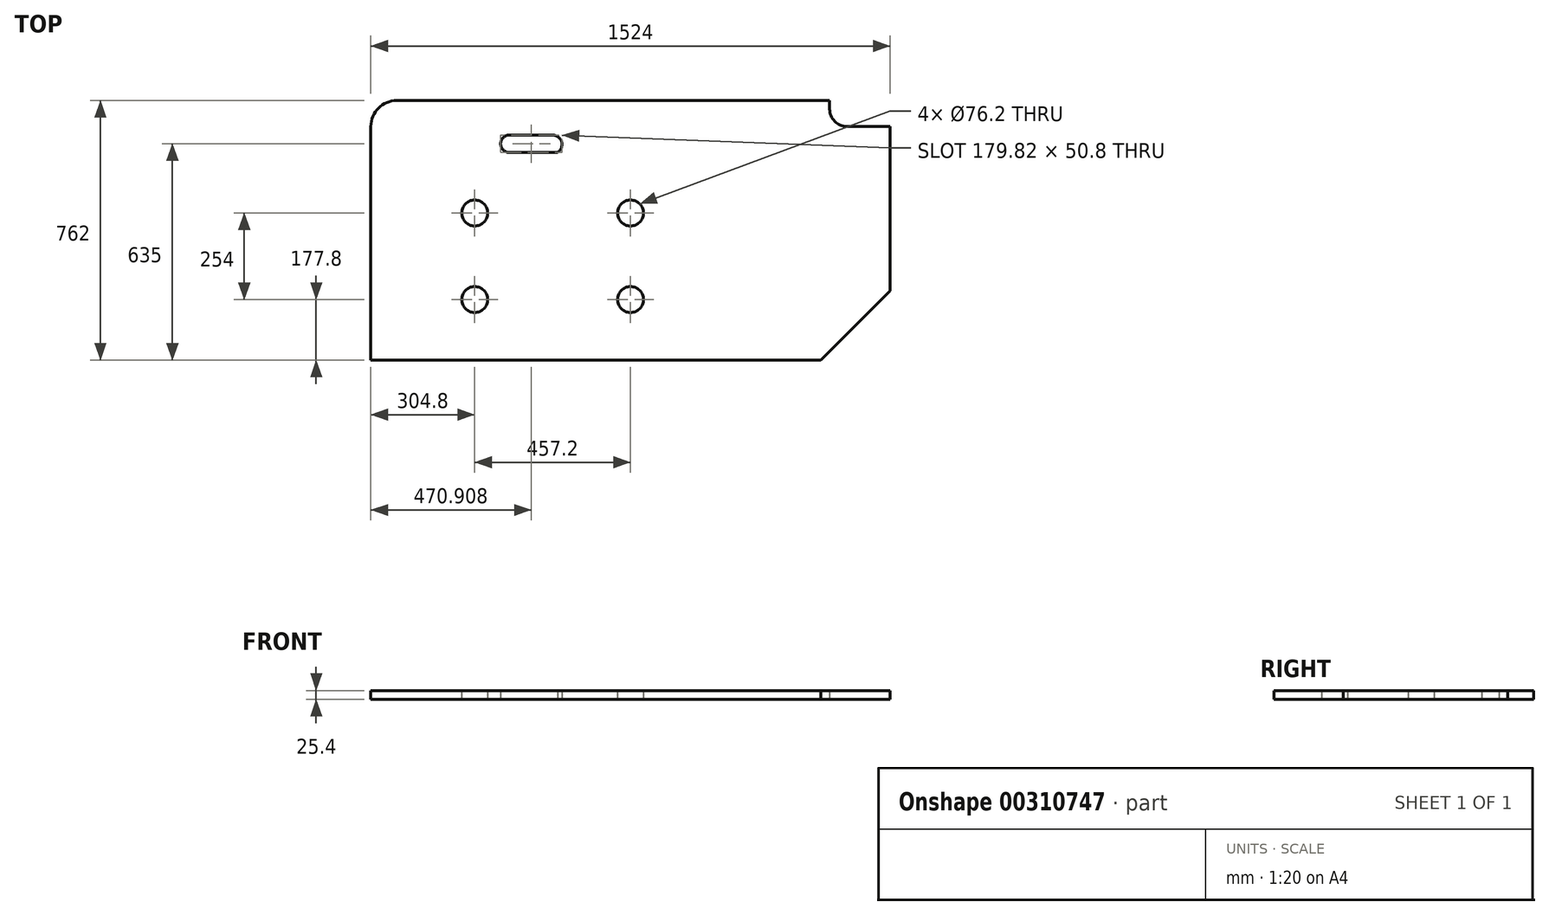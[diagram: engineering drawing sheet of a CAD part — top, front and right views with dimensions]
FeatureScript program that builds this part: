
annotation { "Feature Type Name" : "Feature", "Feature Type Description" : "" }
export const myFeature = defineFeature(function(context is Context, id is Id, definition is map)
    precondition{}
    {
        {
            var Q0;
            Q0=qCreatedBy(makeId("Top.planeOp"),FACE);
            var sketch = newSketch(context, id + "F0", { "sketchPlane" : qUnion([Q0])});
            skPoint(sketch, "E0.0", {"position": v(0, 0) * mm});
            skLineSegment(sketch, "E1.bottom", {"start": v(0, 0) * mm, "end": v(1524, 0) * mm});
            skLineSegment(sketch, "E1.top", {"start": v(0, 762) * mm, "end": v(1346.2, 762) * mm});
            skLineSegment(sketch, "E1.left", {"start": v(0, 0) * mm, "end": v(0, 762) * mm});
            skLineSegment(sketch, "E1.right", {"start": v(1524, 0) * mm, "end": v(1524, 685.8) * mm});
            skLineSegment(sketch, "E2.bottom", {"start": v(304.8, 177.8) * mm, "end": v(762, 177.8) * mm, "construction": true});
            skLineSegment(sketch, "E2.top", {"start": v(304.8, 431.8) * mm, "end": v(762, 431.8) * mm, "construction": true});
            skLineSegment(sketch, "E2.left", {"start": v(304.8, 177.8) * mm, "end": v(304.8, 431.8) * mm, "construction": true});
            skLineSegment(sketch, "E2.right", {"start": v(762, 177.8) * mm, "end": v(762, 431.8) * mm, "construction": true});
            skPoint(sketch, "E3", {"position": v(304.8, 177.8) * mm});
            skPoint(sketch, "E4", {"position": v(304.8, 431.8) * mm});
            skPoint(sketch, "E5", {"position": v(762, 431.8) * mm});
            skPoint(sketch, "E6", {"position": v(762, 177.8) * mm});
            skLineSegment(sketch, "E7", {"start": v(1346.2, 762) * mm, "end": v(1346.2, 685.8) * mm});
            skLineSegment(sketch, "E8", {"start": v(1346.2, 685.8) * mm, "end": v(1524, 685.8) * mm});
            skSolve(sketch);
        }
        {
            var Q0;
            Q0=makeQuery(id+"F0.imprint","IMPRINT",FACE,{"disambiguationData":[TD([[makeQuery(id+"F0.imprint","IMPRINT",EDGE,{"derivedFrom":sQuery(id+"F0.wireOp",EDGE,"E1.bottom")}),1.0]])]});
            extrude(context, id + "F1", {"entities" : qUnion([Q0]), "depth" : 25.4 * mm, "offsetDistance" : 25.4 * mm});
        }
        {
            var Q0;
            Q0=sQuery(id+"F0.wireOp",VERTEX,"E3");
            var Q1;
            Q1=sQuery(id+"F0.wireOp",VERTEX,"E4");
            var Q2;
            Q2=sQuery(id+"F0.wireOp",VERTEX,"E5");
            var Q3;
            Q3=sQuery(id+"F0.wireOp",VERTEX,"E6");
            var Q4;
            Q4=makeQuery(id+"F1.opExtrude","SWEPT_BODY",BODY,{"disambiguationData":[OSD([sQuery(id+"F0.wireOp",EDGE,"E1.bottom"),sQuery(id+"F0.wireOp",EDGE,"E1.top"),sQuery(id+"F0.wireOp",EDGE,"E1.left"),sQuery(id+"F0.wireOp",EDGE,"E1.right")])]});
            hole(context, id + "F2", {"style" : HoleStyle.SIMPLE, "endStyle" : HoleEndStyle.THROUGH, "oppositeDirection" : true, "holeDiameter" : 76.2 * mm, "majorDiameter" : 6.35 * mm, "isTappedThrough" : true, "tappedDepth" : 12.7 * mm, "tapClearance" : 3, "locations" : qUnion([Q0, Q1, Q2, Q3]), "scope" : qUnion([Q4])});
        }
        {
            var Q0;
            Q0=makeQuery(id+"F1.opExtrude","SWEPT_EDGE",EDGE,{"disambiguationData":[OSD([sQuery(id+"F0.wireOp",EDGE,"E1.top"),sQuery(id+"F0.wireOp",EDGE,"E1.left")])]});
            fillet(context, id + "F3", {"entities" : qUnion([Q0]), "tangentPropagation" : true, "radius" : 76.2 * mm, "defaultsChanged" : true, "vertexSettings" : [], "allowEdgeOverflow" : false});
        }
        {
            var Q0;
            Q0=makeQuery(id+"F1.opExtrude","SWEPT_EDGE",EDGE,{"disambiguationData":[OSD([sQuery(id+"F0.wireOp",EDGE,"E1.bottom"),sQuery(id+"F0.wireOp",EDGE,"E1.right")])]});
            chamfer(context, id + "F4", {"entities" : qUnion([Q0]), "width" : 203.2 * mm, "tangentPropagation" : true});
        }
        {
            var Q0;
            Q0=makeQuery(id+"F1.opExtrude","SWEPT_EDGE",EDGE,{"disambiguationData":[OSD([sQuery(id+"F0.wireOp",EDGE,"E7"),sQuery(id+"F0.wireOp",EDGE,"E8")])]});
            fillet(context, id + "F5", {"entities" : qUnion([Q0]), "tangentPropagation" : true, "radius" : 50.8 * mm, "defaultsChanged" : true, "vertexSettings" : [], "allowEdgeOverflow" : false});
        }
        {
            var Q0;
            Q0=qCreatedBy(makeId("Top.planeOp"),FACE);
            var sketch = newSketch(context, id + "F6", { "sketchPlane" : qUnion([Q0])});
            skLineSegment(sketch, "E9.bottom", {"start": v(406.4, 660.4) * mm, "end": v(533.4, 660.4) * mm});
            skLineSegment(sketch, "E9.top", {"start": v(406.4, 609.6) * mm, "end": v(547.82, 609.6) * mm});
            skArc(sketch, "E10", {"start": v(406.4, 660.4) * mm, "mid": v(381, 635) * mm, "end": v(406.4, 609.6) * mm});
            skArc(sketch, "E11", {"start": v(533.4, 660.4) * mm, "mid": v(559.8, 640.45) * mm, "end": v(547.82, 609.6) * mm});
            skSolve(sketch);
        }
        {
            var Q0;
            Q0 = qSketchRegion(id + "F6", true);
            extrude(context, id + "F7", {"entities" : qUnion([Q0]), "operationType" : NewBodyOperationType.REMOVE, "endBound" : BoundingType.THROUGH_ALL, "depth" : 25.4 * mm, "offsetDistance" : 25.4 * mm});
        }
    });
